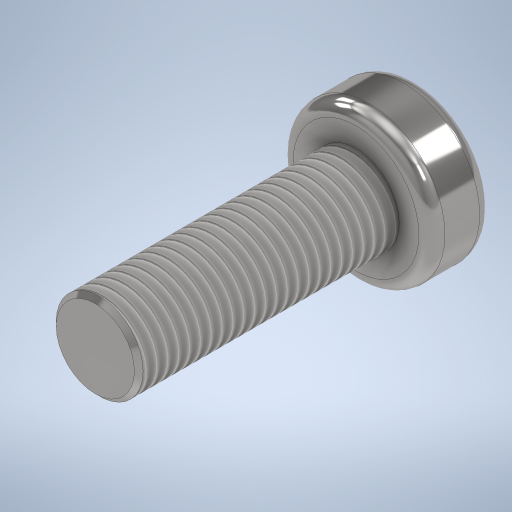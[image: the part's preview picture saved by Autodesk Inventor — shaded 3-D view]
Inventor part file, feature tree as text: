
AUTODESK INVENTOR PART (.ipt)
format: ipt  version: 2023 (Build 270158000, 158)  size: 345,088 bytes
history: native  units: mm
features: extrude x3, other x2, sketch x2, fillet x1, chamfer x1
ambient origin geometry x8: Origin, YZ Plane, XZ Plane, XY Plane, X Axis, Y Axis, Z Axis, Center Point
bodies: Body1 (feature_tree)
feature tree (9):
  other  "솔리드1"
  sketch  "스케치1"
  extrude  "돌출1"  Depth=2.0mm
  extrude  "돌출2"  Depth=6.0mm TaperAngle=0.0deg
  fillet  "모깎기1"  Radius=3.5mm
  extrude  "돌출3"  Depth=1.4mm TaperAngle=0.0deg
  chamfer  "모따기1"  Distance=0.3mm
  other  "스레드1"
  sketch  "스케치2"
